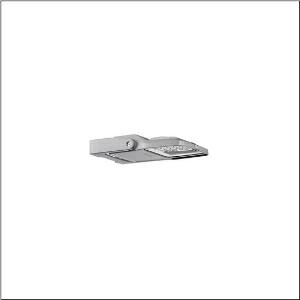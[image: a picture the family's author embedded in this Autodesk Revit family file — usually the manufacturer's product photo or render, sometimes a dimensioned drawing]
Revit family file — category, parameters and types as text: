
# Revit family: floodlight_fl_21_iq_micro___pl61_5xa7762a2c2a_d8df
name_source: partatom
category: Lighting Fixtures
units: mm (PartAtom-declared; Revit-internal decimal feet)

## family parameters
Cut with Voids When Loaded = No
Host = Face
Light Source = No
Part Type = Normal
Room Calculation Point = No
Round Connector Dimension = Use Diameter
Shared = No

## types (1)
- --- (1 x LED, 2910 lm, 23.1 W, 3000K)
    Apparent Load = 23 VA
    CIE Flux Codes = 33 65 98 100 100
    Color Rendering = 70
    Color Temperature = 3000K
    Default Elevation = 1800 mm
    Description = Floodlight FL 21 iQ micro, floodlight, primary light control with lens, of PMMA, primary optical cover: protective disc, of toughened safety glass, transparent, light distribution: PL61, light emission: direct distribution, installation type: surface-mounted, LED, High Power LED, rated luminous flux: 2.910lm, luminous efficacy: 126lm/W, light colour: 730, colour temperature: 3000K, control: Auto-Match, Temp-Guard, Night-Set, Smart-Wire, Desk-Remote (wireless, voltage-free reading and setting of iQ features in the workshop via application-optimized NFC function/RFID function), optimised constant luminous flux control (CLO 2.0), Street-Remote, with terminal, 6-pole, mains connection: 220..240V, AC, 50/60Hz, start of lifetime: 23W, end of service life: 24W, reduction: 11W, luminaire housing, of diecast aluminium, powder-coated, Siteco® metallic grey (DB 702S), corrosivity category C5 mid according to DIN EN ISO 12944, sealing non-destructively replaceable, design bracket, of diecast aluminium, powder-coated, Siteco® metallic grey (DB 702S), protection rating (complete): IP66, insulation class (complete): insulation class II (safety insulation), certification: CE, ENEC, VDE, protection symbol: D, impact resistance: IK07, permissible operating ambient temperature: -40..+40°C, permissible operating ambient temperature for outdoor applications: -40..+50°C, standard: DIN EN 12944, LABS conformity tested according to VDMA 24364:2018-05, packaging unit: 1 piece

Light Distribution: PL61
    Height = 65 mm
    Lamp = 1 x LED
    Lamp Light Flux = 2910 lm
    Lamp Power = 23.1 W
    Lamp count = 1
    Length = 312 mm
    Luminous efficacy = 126 lm/W
    Manufacturer = Siteco
    ModVariant = No
    Model = 5XA7762A2C2A
    Mounting Place = Wall
    Mounting Type = Surface mounted
    Number of Poles = 1
    OnlyDefault = Yes
    Power Factor = 1
    Product Name = Floodlight FL 21 iQ micro | PL61
    Product group = floodlight | wall mounted
    ProductGroupID = 2001
    Protection Class = Protection class II
    Protection Degree = IP 66
    RLX_Detail_Level = 1
    RLX_Emergency_Light_Flux = 0 lm
    RLX_Emergency_Type = 0
    RLX_Emergency_Type_DB = No
    RlxData = <blob elided: 97421 chars, md5=987aaa2b>
    Socket = socket
    Standby Power = 0 W
    System Light Flux = 2910 lm
    System Power = 23 W
    Type Comments = factory setting: luminous flux: 100 % | dim-lin: 254 | 455 mA
    Type Image = l_1006878.jpg
    URL = http://relux.com
    VarID = @adj_167089
    Voltage = 0 V
    Weight = 0.00 kg
    Width = 230 mm

## geometry (parser evidence)
native form markers: Blend x4, Sweep x11
no freeform markers — native parametric forms only
